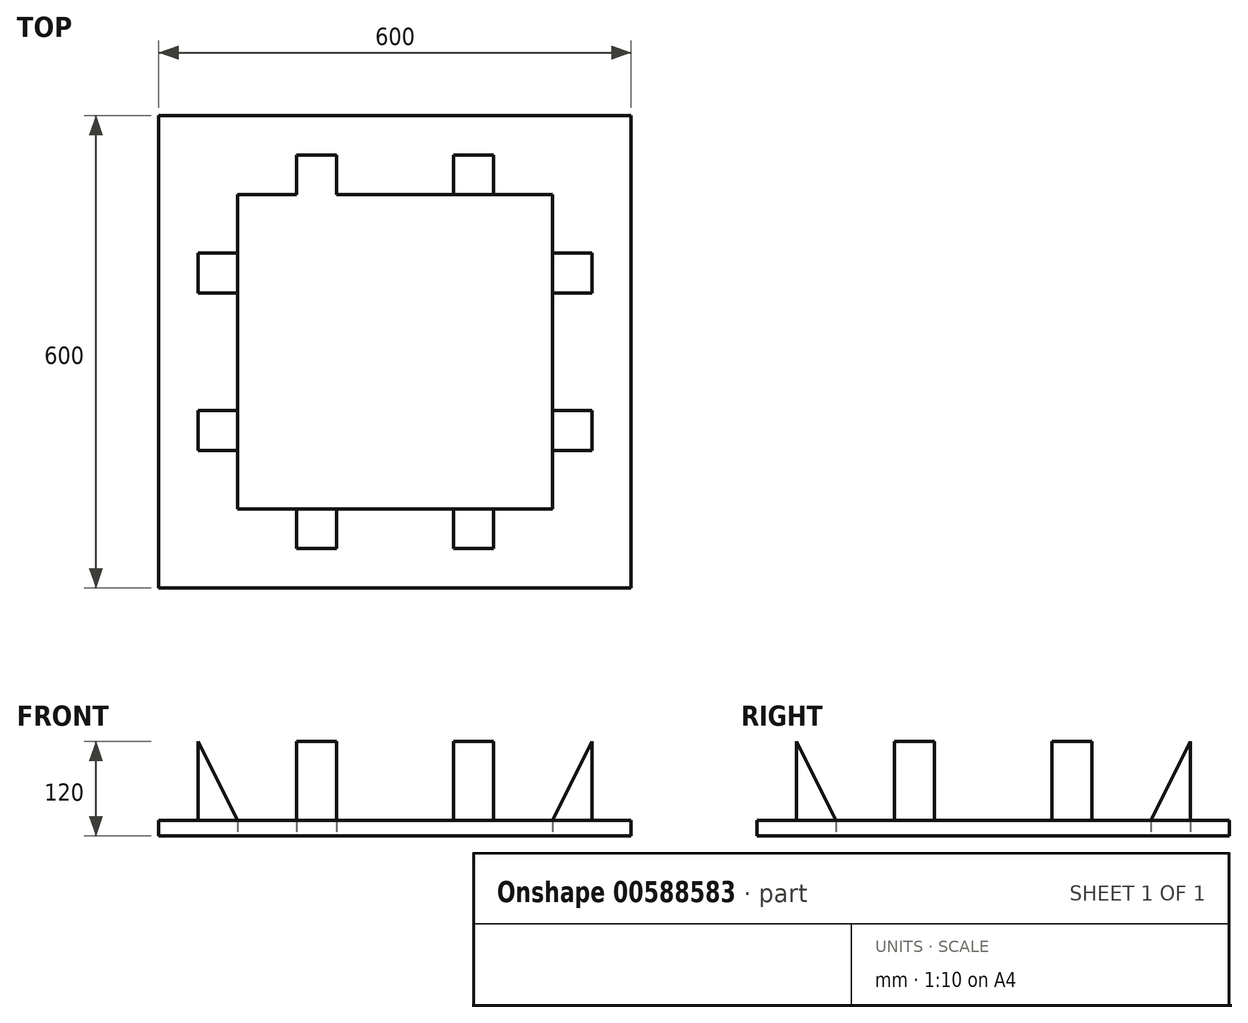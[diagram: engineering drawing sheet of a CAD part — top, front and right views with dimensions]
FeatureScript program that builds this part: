
annotation { "Feature Type Name" : "Feature", "Feature Type Description" : "" }
export const myFeature = defineFeature(function(context is Context, id is Id, definition is map)
    precondition{}
    {
        {
            var Q0;
            Q0=qCreatedBy(makeId("Top.planeOp"),FACE);
            var sketch = newSketch(context, id + "F0", { "sketchPlane" : qUnion([Q0])});
            skLineSegment(sketch, "E0.top", {"start": v(-357.84, -313.78) * mm, "end": v(242.16, -313.78) * mm});
            skLineSegment(sketch, "E0.right", {"start": v(242.16, 286.22) * mm, "end": v(242.16, -313.78) * mm});
            skLineSegment(sketch, "E1", {"start": v(-357.84, 286.22) * mm, "end": v(-357.84, -313.78) * mm});
            skLineSegment(sketch, "E2", {"start": v(-357.84, 286.22) * mm, "end": v(242.16, 286.22) * mm});
            skLineSegment(sketch, "E3.bottom", {"start": v(-257.84, 186.22) * mm, "end": v(142.16, 186.22) * mm});
            skLineSegment(sketch, "E3.top", {"start": v(-257.84, -213.78) * mm, "end": v(142.16, -213.78) * mm});
            skLineSegment(sketch, "E3.left", {"start": v(-257.84, 186.22) * mm, "end": v(-257.84, -213.78) * mm});
            skLineSegment(sketch, "E3.right", {"start": v(142.16, 186.22) * mm, "end": v(142.16, -213.78) * mm});
            skLineSegment(sketch, "E4", {"start": v(-257.84, 186.22) * mm, "end": v(-257.84, -13.78) * mm});
            skLineSegment(sketch, "E5", {"start": v(-257.84, -13.78) * mm, "end": v(-257.84, -213.78) * mm});
            skLineSegment(sketch, "E6.top", {"start": v(-157.84, 236.22) * mm, "end": v(-132.44, 236.22) * mm});
            skLineSegment(sketch, "E6.right", {"start": v(-132.44, 186.22) * mm, "end": v(-132.44, 236.22) * mm});
            skLineSegment(sketch, "E7.bottom", {"start": v(-132.44, 236.22) * mm, "end": v(-183.24, 236.22) * mm});
            skLineSegment(sketch, "E7.left", {"start": v(-132.44, 236.22) * mm, "end": v(-132.44, 186.22) * mm});
            skLineSegment(sketch, "E7.right", {"start": v(-183.24, 236.22) * mm, "end": v(-183.24, 186.22) * mm});
            skLineSegment(sketch, "E8.bottom", {"start": v(67.56, 236.22) * mm, "end": v(16.76, 236.22) * mm});
            skLineSegment(sketch, "E8.left", {"start": v(67.56, 236.22) * mm, "end": v(67.56, 186.22) * mm});
            skLineSegment(sketch, "E8.right", {"start": v(16.76, 236.22) * mm, "end": v(16.76, 186.22) * mm});
            skLineSegment(sketch, "E9.right", {"start": v(67.56, -213.78) * mm, "end": v(67.56, -263.78) * mm});
            skLineSegment(sketch, "E10.bottom", {"start": v(67.56, -263.78) * mm, "end": v(16.76, -263.78) * mm});
            skLineSegment(sketch, "E10.left", {"start": v(67.56, -263.78) * mm, "end": v(67.56, -213.78) * mm});
            skLineSegment(sketch, "E10.right", {"start": v(16.76, -263.78) * mm, "end": v(16.76, -213.78) * mm});
            skLineSegment(sketch, "E11.bottom", {"start": v(-132.44, -213.78) * mm, "end": v(-183.24, -213.78) * mm});
            skLineSegment(sketch, "E11.top", {"start": v(-132.44, -263.78) * mm, "end": v(-183.24, -263.78) * mm});
            skLineSegment(sketch, "E11.left", {"start": v(-132.44, -213.78) * mm, "end": v(-132.44, -263.78) * mm});
            skLineSegment(sketch, "E11.right", {"start": v(-183.24, -213.78) * mm, "end": v(-183.24, -263.78) * mm});
            skLineSegment(sketch, "E12.top", {"start": v(142.16, 111.62) * mm, "end": v(192.16, 111.62) * mm});
            skLineSegment(sketch, "E13.bottom", {"start": v(192.16, 111.62) * mm, "end": v(142.16, 111.62) * mm});
            skLineSegment(sketch, "E13.top", {"start": v(192.16, 60.82) * mm, "end": v(142.16, 60.82) * mm});
            skLineSegment(sketch, "E13.left", {"start": v(192.16, 111.62) * mm, "end": v(192.16, 60.82) * mm});
            skLineSegment(sketch, "E14.bottom", {"start": v(-307.84, -139.18) * mm, "end": v(-257.84, -139.18) * mm});
            skLineSegment(sketch, "E14.top", {"start": v(-307.84, -88.38) * mm, "end": v(-257.84, -88.38) * mm});
            skLineSegment(sketch, "E15", {"start": v(-307.84, -88.38) * mm, "end": v(-307.84, -139.18) * mm});
            skLineSegment(sketch, "E16.bottom", {"start": v(142.16, -139.18) * mm, "end": v(192.16, -139.18) * mm});
            skLineSegment(sketch, "E16.top", {"start": v(142.16, -88.38) * mm, "end": v(192.16, -88.38) * mm});
            skLineSegment(sketch, "E16.left", {"start": v(142.16, -139.18) * mm, "end": v(142.16, -88.38) * mm});
            skLineSegment(sketch, "E16.right", {"start": v(192.16, -139.18) * mm, "end": v(192.16, -88.38) * mm});
            skPoint(sketch, "E17.firstSnap0", {"position": v(167.16, 60.82) * mm});
            skLineSegment(sketch, "E17.bottom", {"start": v(-257.84, 60.82) * mm, "end": v(-307.84, 60.82) * mm});
            skLineSegment(sketch, "E17.top", {"start": v(-257.84, 111.62) * mm, "end": v(-307.84, 111.62) * mm});
            skLineSegment(sketch, "E17.left", {"start": v(-257.84, 60.82) * mm, "end": v(-257.84, 111.62) * mm});
            skLineSegment(sketch, "E17.right", {"start": v(-307.84, 60.82) * mm, "end": v(-307.84, 111.62) * mm});
            skSolve(sketch);
        }
        {
            var Q0;
            Q0 = qSketchRegion(id + "F0", true);
            var Q1;
            Q1=makeQuery(id+"F0.imprint","IMPRINT",FACE,{"disambiguationData":[TD([[makeQuery(id+"F0.imprint","IMPRINT",EDGE,{"derivedFrom":sQuery(id+"F0.wireOp",EDGE,"4075ac3e-ca4d-41d2-80bb-f85553625f92.left")}),1.0]])]});
            extrude(context, id + "F1", {"entities" : qUnion([Q0, Q1]), "depth" : 20 * mm, "offsetDistance" : 25 * mm});
        }
        {
            var Q0;
            Q0=makeQuery(id+"F1.opExtrude","SWEPT_FACE",FACE,{"disambiguationData":[OSD([sQuery(id+"F0.wireOp",EDGE,"E14.top")])]});
            var sketch = newSketch(context, id + "F2", { "sketchPlane" : qUnion([Q0])});
            skLineSegment(sketch, "E18.bottom", {"start": v(-257.84, 20) * mm, "end": v(-307.84, 20) * mm});
            skLineSegment(sketch, "E18.right", {"start": v(-307.84, 20) * mm, "end": v(-307.84, 120) * mm});
            skLineSegment(sketch, "E19", {"start": v(-257.84, 20) * mm, "end": v(-307.84, 120) * mm});
            skSolve(sketch);
        }
        {
            var Q0;
            Q0=makeQuery(id+"F1.opExtrude","SWEPT_FACE",FACE,{"disambiguationData":[OSD([sQuery(id+"F0.wireOp",EDGE,"E17.top")])]});
            var sketch = newSketch(context, id + "F3", { "sketchPlane" : qUnion([Q0])});
            skLineSegment(sketch, "E20.bottom", {"start": v(-257.84, 20) * mm, "end": v(-307.84, 20) * mm});
            skLineSegment(sketch, "E20.right", {"start": v(-307.84, 20) * mm, "end": v(-307.84, 120) * mm});
            skLineSegment(sketch, "E21", {"start": v(-257.84, 20) * mm, "end": v(-307.84, 120) * mm});
            skSolve(sketch);
        }
        {
            var Q0;
            Q0=makeQuery(id+"F1.opExtrude","SWEPT_FACE",FACE,{"disambiguationData":[OSD([sQuery(id+"F0.wireOp",EDGE,"E7.left")])]});
            var sketch = newSketch(context, id + "F4", { "sketchPlane" : qUnion([Q0])});
            skLineSegment(sketch, "E22.bottom", {"start": v(-186.22, 20) * mm, "end": v(-236.22, 20) * mm});
            skLineSegment(sketch, "E22.right", {"start": v(-236.22, 20) * mm, "end": v(-236.22, 120) * mm});
            skLineSegment(sketch, "E23", {"start": v(-186.22, 20) * mm, "end": v(-236.22, 120) * mm});
            skSolve(sketch);
        }
        {
            var Q0;
            Q0=makeQuery(id+"F1.opExtrude","SWEPT_FACE",FACE,{"disambiguationData":[OSD([sQuery(id+"F0.wireOp",EDGE,"E8.left")])]});
            var sketch = newSketch(context, id + "F5", { "sketchPlane" : qUnion([Q0])});
            skLineSegment(sketch, "E24.bottom", {"start": v(-186.22, 20) * mm, "end": v(-236.22, 20) * mm});
            skLineSegment(sketch, "E24.right", {"start": v(-236.22, 20) * mm, "end": v(-236.22, 120) * mm});
            skLineSegment(sketch, "E25", {"start": v(-186.22, 20) * mm, "end": v(-236.22, 120) * mm});
            skSolve(sketch);
        }
        {
            var Q0;
            Q0=makeQuery(id+"F1.opExtrude","SWEPT_FACE",FACE,{"disambiguationData":[OSD([sQuery(id+"F0.wireOp",EDGE,"E13.top")])]});
            var sketch = newSketch(context, id + "F6", { "sketchPlane" : qUnion([Q0])});
            skLineSegment(sketch, "E26.bottom", {"start": v(-142.16, 20) * mm, "end": v(-192.16, 20) * mm});
            skLineSegment(sketch, "E26.right", {"start": v(-192.16, 20) * mm, "end": v(-192.16, 120) * mm});
            skLineSegment(sketch, "E27", {"start": v(-142.16, 20) * mm, "end": v(-192.16, 120) * mm});
            skSolve(sketch);
        }
        {
            var Q0;
            Q0=makeQuery(id+"F1.opExtrude","SWEPT_FACE",FACE,{"disambiguationData":[OSD([sQuery(id+"F0.wireOp",EDGE,"E16.bottom")])]});
            var sketch = newSketch(context, id + "F7", { "sketchPlane" : qUnion([Q0])});
            skLineSegment(sketch, "E28.bottom", {"start": v(-142.16, 20) * mm, "end": v(-192.16, 20) * mm});
            skLineSegment(sketch, "E28.right", {"start": v(-192.16, 20) * mm, "end": v(-192.16, 120) * mm});
            skLineSegment(sketch, "E29", {"start": v(-142.16, 20) * mm, "end": v(-192.16, 120) * mm});
            skSolve(sketch);
        }
        {
            var Q0;
            Q0=makeQuery(id+"F2.imprint","IMPRINT",FACE,{"disambiguationData":[TD([[makeQuery(id+"F2.imprint","IMPRINT",EDGE,{"derivedFrom":sQuery(id+"F2.wireOp",EDGE,"E18.bottom")}),1.0]])]});
            var Q1;
            Q1=makeQuery(id+"F3.imprint","IMPRINT",FACE,{"disambiguationData":[TD([[makeQuery(id+"F3.imprint","IMPRINT",EDGE,{"derivedFrom":sQuery(id+"F3.wireOp",EDGE,"E20.bottom")}),-1.0]])]});
            var Q2;
            Q2=makeQuery(id+"F3.imprint","IMPRINT",FACE,{"disambiguationData":[TD([[makeQuery(id+"F3.imprint","IMPRINT",EDGE,{"derivedFrom":sQuery(id+"F3.wireOp",EDGE,"E20.bottom")}),1.0]])]});
            var Q3;
            Q3=makeQuery(id+"F2.imprint","IMPRINT",FACE,{"disambiguationData":[TD([[makeQuery(id+"F2.imprint","IMPRINT",EDGE,{"derivedFrom":sQuery(id+"F2.wireOp",EDGE,"E18.bottom")}),-1.0]])]});
            extrude(context, id + "F8", {"entities" : qUnion([Q0, Q1, Q2, Q3]), "operationType" : NewBodyOperationType.ADD, "depth" : 50.8 * mm, "offsetDistance" : 25 * mm});
        }
        {
            var Q0;
            Q0=makeQuery(id+"F1.opExtrude","SWEPT_FACE",FACE,{"disambiguationData":[OSD([sQuery(id+"F0.wireOp",EDGE,"E10.right")])]});
            var sketch = newSketch(context, id + "F9", { "sketchPlane" : qUnion([Q0])});
            skLineSegment(sketch, "E30.bottom", {"start": v(-213.78, 20) * mm, "end": v(-263.78, 20) * mm});
            skLineSegment(sketch, "E30.right", {"start": v(-263.78, 20) * mm, "end": v(-263.78, 120) * mm});
            skLineSegment(sketch, "E31", {"start": v(-213.78, 20) * mm, "end": v(-263.78, 120) * mm});
            skSolve(sketch);
        }
        {
            var Q0;
            Q0=makeQuery(id+"F1.opExtrude","SWEPT_FACE",FACE,{"disambiguationData":[OSD([sQuery(id+"F0.wireOp",EDGE,"E11.right")])]});
            var sketch = newSketch(context, id + "F10", { "sketchPlane" : qUnion([Q0])});
            skLineSegment(sketch, "E32.bottom", {"start": v(-213.78, 20) * mm, "end": v(-263.78, 20) * mm});
            skLineSegment(sketch, "E32.right", {"start": v(-263.78, 20) * mm, "end": v(-263.78, 120) * mm});
            skLineSegment(sketch, "E33", {"start": v(-213.78, 20) * mm, "end": v(-263.78, 120) * mm});
            skSolve(sketch);
        }
        {
            var Q0;
            Q0=makeQuery(id+"F4.imprint","IMPRINT",FACE,{"disambiguationData":[TD([[makeQuery(id+"F4.imprint","IMPRINT",EDGE,{"derivedFrom":sQuery(id+"F4.wireOp",EDGE,"E22.bottom")}),-1.0]])]});
            var Q1;
            Q1=makeQuery(id+"F4.imprint","IMPRINT",FACE,{"disambiguationData":[TD([[makeQuery(id+"F4.imprint","IMPRINT",EDGE,{"derivedFrom":sQuery(id+"F4.wireOp",EDGE,"E22.bottom")}),1.0]])]});
            var Q2;
            Q2=makeQuery(id+"F5.imprint","IMPRINT",FACE,{"disambiguationData":[TD([[makeQuery(id+"F5.imprint","IMPRINT",EDGE,{"derivedFrom":sQuery(id+"F5.wireOp",EDGE,"E24.bottom")}),-1.0]])]});
            var Q3;
            Q3=makeQuery(id+"F5.imprint","IMPRINT",FACE,{"disambiguationData":[TD([[makeQuery(id+"F5.imprint","IMPRINT",EDGE,{"derivedFrom":sQuery(id+"F5.wireOp",EDGE,"E24.bottom")}),1.0]])]});
            extrude(context, id + "F11", {"entities" : qUnion([Q0, Q1, Q2, Q3]), "operationType" : NewBodyOperationType.ADD, "depth" : 50.8 * mm, "offsetDistance" : 25 * mm});
        }
        {
            var Q0;
            Q0=makeQuery(id+"F6.imprint","IMPRINT",FACE,{"disambiguationData":[TD([[makeQuery(id+"F6.imprint","IMPRINT",EDGE,{"derivedFrom":sQuery(id+"F6.wireOp",EDGE,"E26.bottom")}),-1.0]])]});
            var Q1;
            Q1=makeQuery(id+"F6.imprint","IMPRINT",FACE,{"disambiguationData":[TD([[makeQuery(id+"F6.imprint","IMPRINT",EDGE,{"derivedFrom":sQuery(id+"F6.wireOp",EDGE,"E26.bottom")}),1.0]])]});
            var Q2;
            Q2=makeQuery(id+"F7.imprint","IMPRINT",FACE,{"disambiguationData":[TD([[makeQuery(id+"F7.imprint","IMPRINT",EDGE,{"derivedFrom":sQuery(id+"F7.wireOp",EDGE,"E28.bottom")}),1.0]])]});
            var Q3;
            Q3=makeQuery(id+"F7.imprint","IMPRINT",FACE,{"disambiguationData":[TD([[makeQuery(id+"F7.imprint","IMPRINT",EDGE,{"derivedFrom":sQuery(id+"F7.wireOp",EDGE,"E28.bottom")}),-1.0]])]});
            extrude(context, id + "F12", {"entities" : qUnion([Q0, Q1, Q2, Q3]), "operationType" : NewBodyOperationType.ADD, "depth" : 50.8 * mm, "offsetDistance" : 25 * mm});
        }
        {
            var Q0;
            Q0=makeQuery(id+"F9.imprint","IMPRINT",FACE,{"disambiguationData":[TD([[makeQuery(id+"F9.imprint","IMPRINT",EDGE,{"derivedFrom":sQuery(id+"F9.wireOp",EDGE,"E30.bottom")}),-1.0]])]});
            var Q1;
            Q1=makeQuery(id+"F9.imprint","IMPRINT",FACE,{"disambiguationData":[TD([[makeQuery(id+"F9.imprint","IMPRINT",EDGE,{"derivedFrom":sQuery(id+"F9.wireOp",EDGE,"E30.bottom")}),1.0]])]});
            var Q2;
            Q2=makeQuery(id+"F10.imprint","IMPRINT",FACE,{"disambiguationData":[TD([[makeQuery(id+"F10.imprint","IMPRINT",EDGE,{"derivedFrom":sQuery(id+"F10.wireOp",EDGE,"E32.bottom")}),1.0]])]});
            var Q3;
            Q3=makeQuery(id+"F10.imprint","IMPRINT",FACE,{"disambiguationData":[TD([[makeQuery(id+"F10.imprint","IMPRINT",EDGE,{"derivedFrom":sQuery(id+"F10.wireOp",EDGE,"E32.bottom")}),-1.0]])]});
            extrude(context, id + "F13", {"entities" : qUnion([Q0, Q1, Q2, Q3]), "operationType" : NewBodyOperationType.ADD, "depth" : 50.8 * mm, "offsetDistance" : 25 * mm});
        }
    });
